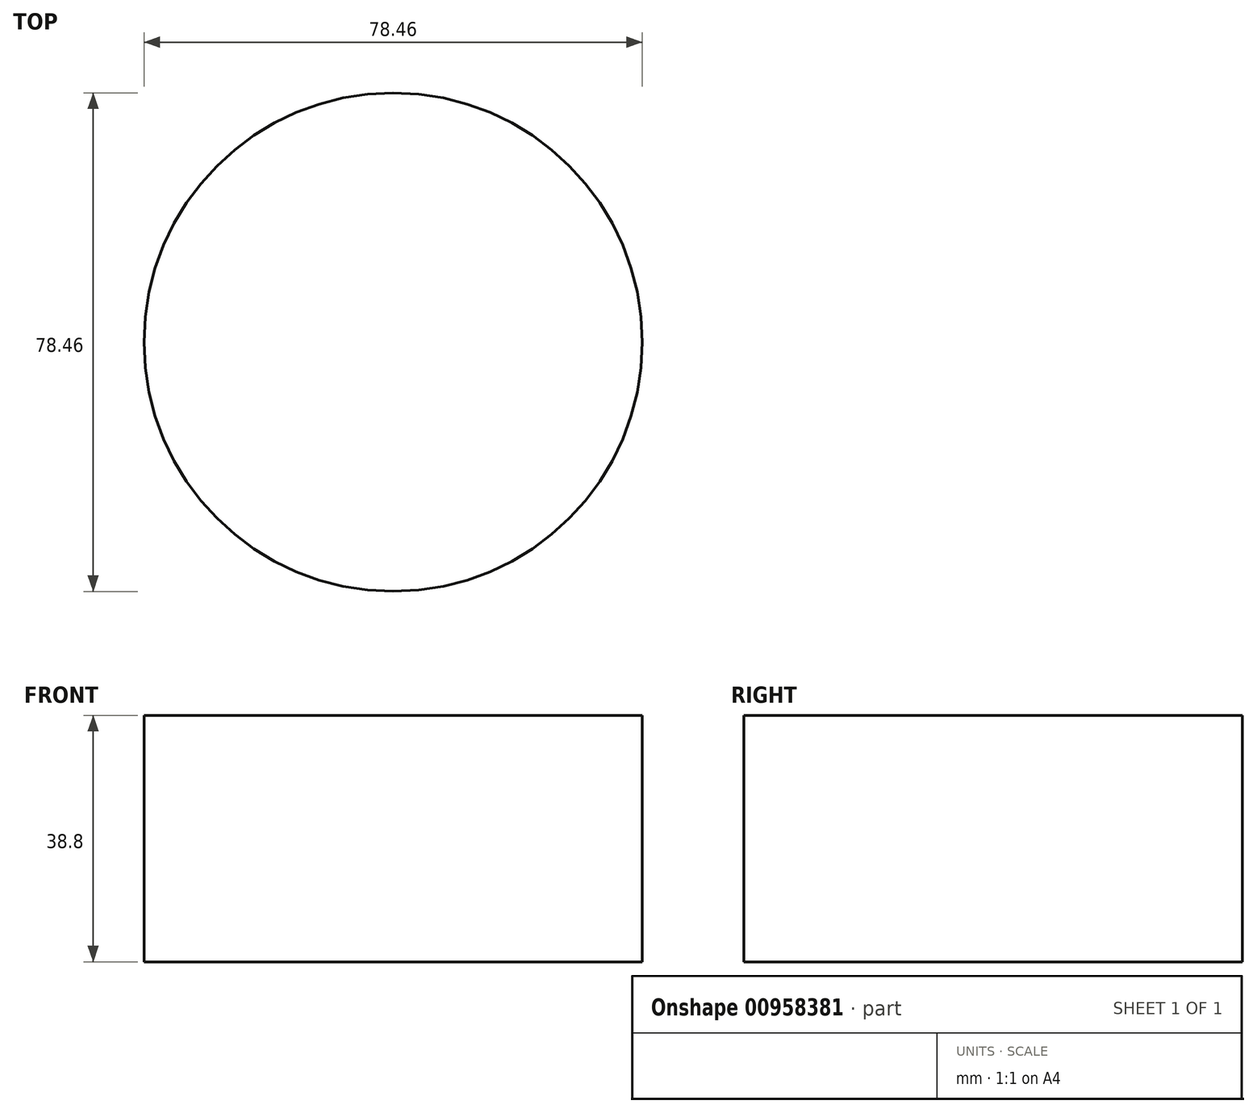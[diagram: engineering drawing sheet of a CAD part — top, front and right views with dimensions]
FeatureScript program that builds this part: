
annotation { "Feature Type Name" : "Feature", "Feature Type Description" : "" }
export const myFeature = defineFeature(function(context is Context, id is Id, definition is map)
    precondition{}
    {
        {
            var Q0;
            Q0=qCreatedBy(makeId("Front.planeOp"),FACE);
            var sketch = newSketch(context, id + "F0", { "sketchPlane" : qUnion([Q0])});
            skLineSegment(sketch, "E0", {"start": v(0, 21.24) * mm, "end": v(-39.23, 21.24) * mm});
            skLineSegment(sketch, "E1", {"start": v(-39.23, 21.24) * mm, "end": v(-39.23, -17.56) * mm});
            skLineSegment(sketch, "E2", {"start": v(-39.23, -17.56) * mm, "end": v(0, -17.56) * mm});
            skLineSegment(sketch, "E3", {"start": v(0, -17.56) * mm, "end": v(0, 21.24) * mm});
            skLineSegment(sketch, "E4", {"start": v(0, 53.81) * mm, "end": v(0, -41.35) * mm, "construction": true});
            skSolve(sketch);
        }
        {
            var Q0;
            Q0 = qSketchRegion(id + "F0", true);
            var Q1;
            Q1=sQuery(id+"F0.wireOp",EDGE,"E4");
            revolve(context, id + "F1", {"surfaceOperationType" : NewSurfaceOperationType.NEW, "entities" : qUnion([Q0]), "axis" : qUnion([Q1]), "revolveType" : RevolveType.FULL});
        }
    });
